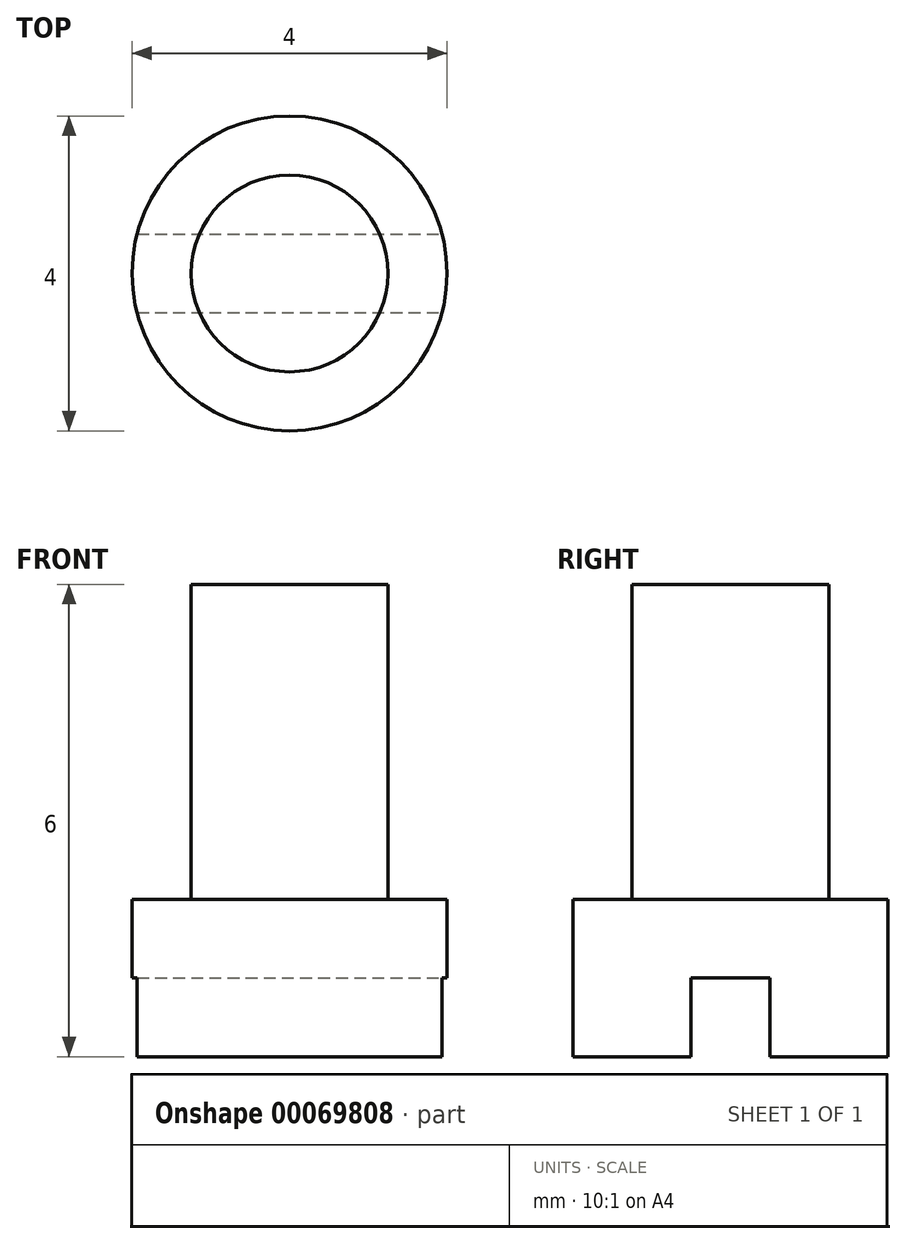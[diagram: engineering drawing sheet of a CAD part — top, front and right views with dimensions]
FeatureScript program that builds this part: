
annotation { "Feature Type Name" : "Feature", "Feature Type Description" : "" }
export const myFeature = defineFeature(function(context is Context, id is Id, definition is map)
    precondition{}
    {
        {
            var Q0;
            Q0=qCreatedBy(makeId("Front.planeOp"),FACE);
            var sketch = newSketch(context, id + "F0", { "sketchPlane" : qUnion([Q0])});
            skLineSegment(sketch, "E0", {"start": v(0, 0) * mm, "end": v(0, 6) * mm, "construction": true});
            skLineSegment(sketch, "E1", {"start": v(0, 0) * mm, "end": v(2, 0) * mm});
            skLineSegment(sketch, "E2", {"start": v(2, 0) * mm, "end": v(2, 2) * mm});
            skLineSegment(sketch, "E3", {"start": v(2, 2) * mm, "end": v(1.25, 2) * mm});
            skLineSegment(sketch, "E4", {"start": v(1.25, 2) * mm, "end": v(1.25, 6) * mm});
            skLineSegment(sketch, "E5", {"start": v(1.25, 6) * mm, "end": v(0, 6) * mm});
            skLineSegment(sketch, "E6", {"start": v(0, 0) * mm, "end": v(0, 6) * mm});
            skSolve(sketch);
        }
        {
            var Q0;
            Q0=makeQuery(id+"F0.imprint","IMPRINT",FACE,{"disambiguationData":[TD([[makeQuery(id+"F0.imprint","IMPRINT",EDGE,{"derivedFrom":sQuery(id+"F0.wireOp",EDGE,"E1")}),1.0]])]});
            var Q1;
            Q1=sQuery(id+"F0.wireOp",EDGE,"E6");
            revolve(context, id + "F1", {"entities" : qUnion([Q0]), "axis" : qUnion([Q1]), "revolveType" : RevolveType.FULL});
        }
        {
            var Q0;
            Q0=makeQuery(id+"F1.opRevolve","SWEPT_FACE",FACE,{"disambiguationData":[OSD([sQuery(id+"F0.wireOp",EDGE,"E1")])]});
            var sketch = newSketch(context, id + "F2", { "sketchPlane" : qUnion([Q0])});
            skLineSegment(sketch, "E7", {"start": v(-1.94, 0.5) * mm, "end": v(1.94, 0.5) * mm});
            skLineSegment(sketch, "E8", {"start": v(-1.94, -0.5) * mm, "end": v(1.94, -0.5) * mm});
            skArc(sketch, "E9", {"start": v(-1.94, 0.5) * mm, "mid": v(-2, 0) * mm, "end": v(-1.94, -0.5) * mm});
            skArc(sketch, "E10.trimOffspring", {"start": v(1.94, -0.5) * mm, "mid": v(2, 0) * mm, "end": v(1.94, 0.5) * mm});
            skSolve(sketch);
        }
        {
            var Q0;
            Q0 = qSketchRegion(id + "F2", true);
            extrude(context, id + "F3", {"entities" : qUnion([Q0]), "operationType" : NewBodyOperationType.REMOVE, "oppositeDirection" : true, "depth" : 1 * mm});
        }
    });
